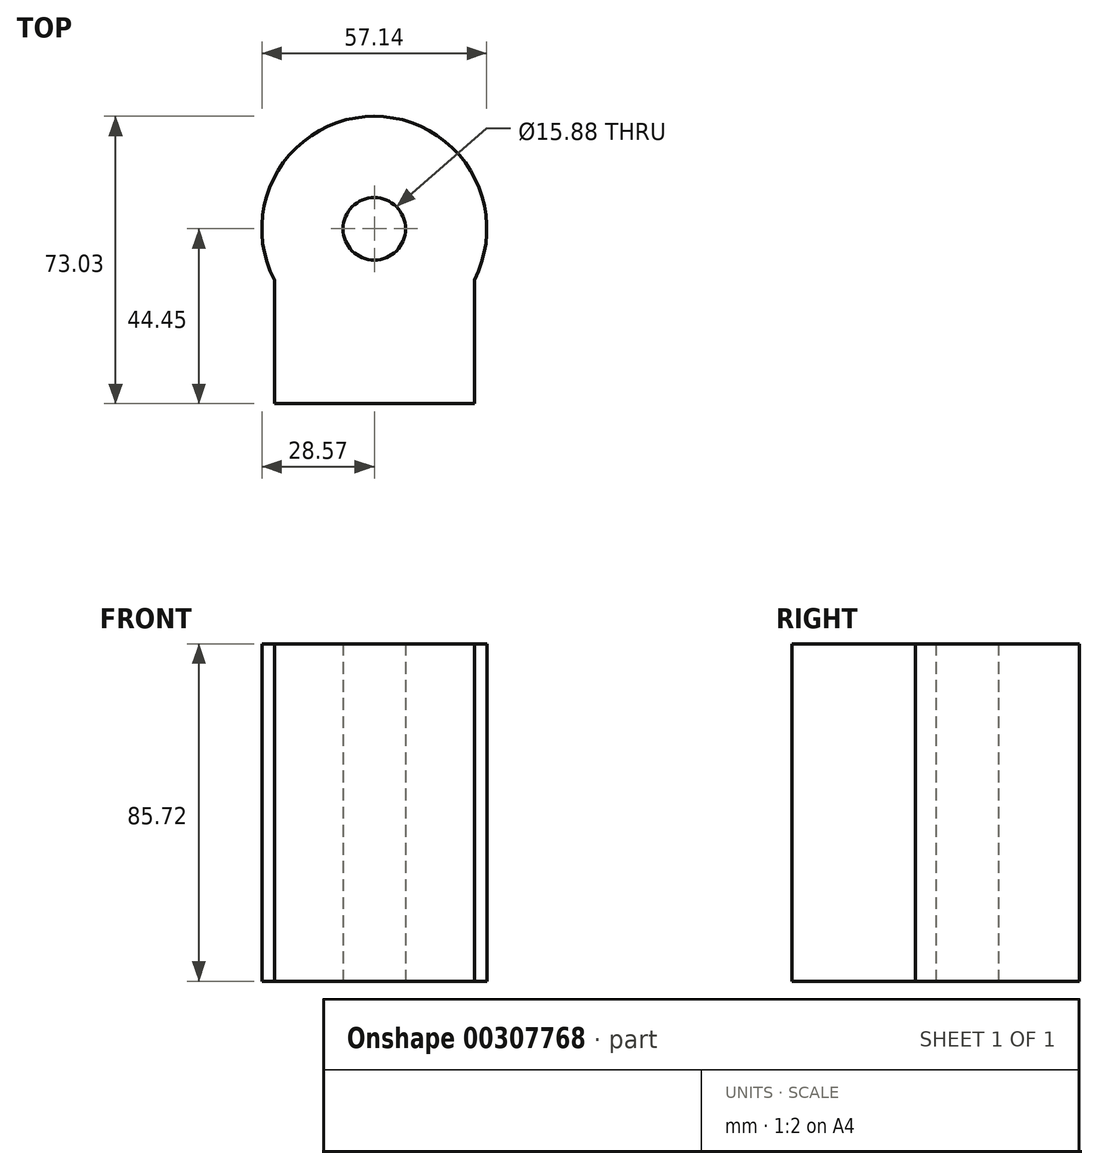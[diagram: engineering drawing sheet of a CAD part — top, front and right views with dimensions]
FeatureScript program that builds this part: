
annotation { "Feature Type Name" : "Feature", "Feature Type Description" : "" }
export const myFeature = defineFeature(function(context is Context, id is Id, definition is map)
    precondition{}
    {
        {
            var Q0;
            Q0=qCreatedBy(makeId("Top.planeOp"),FACE);
            var sketch = newSketch(context, id + "F0", { "sketchPlane" : qUnion([Q0])});
            skArc(sketch, "E0", {"start": v(25.4, -13.1) * mm, "mid": v(0, 28.57) * mm, "end": v(-25.4, -13.1) * mm});
            skCircle(sketch, "E1", {"center": v(0, 0) * mm, "radius": 7.94 * mm});
            skLineSegment(sketch, "E2", {"start": v(0, 0) * mm, "end": v(0, -7.94) * mm});
            skLineSegment(sketch, "E3", {"start": v(-25.4, -44.45) * mm, "end": v(25.4, -44.45) * mm});
            skLineSegment(sketch, "E4", {"start": v(-25.4, -44.45) * mm, "end": v(-25.4, -13.1) * mm});
            skLineSegment(sketch, "E5", {"start": v(25.4, -44.45) * mm, "end": v(25.4, -13.1) * mm});
            skPoint(sketch, "E6.orphan", {"position": v(0, -44.45) * mm});
            skSolve(sketch);
        }
        {
            var Q0;
            Q0 = qSketchRegion(id + "F0", true);
            extrude(context, id + "F1", {"entities" : qUnion([Q0]), "endBound" : BoundingType.SYMMETRIC, "depth" : 85.72 * mm});
        }
    });
